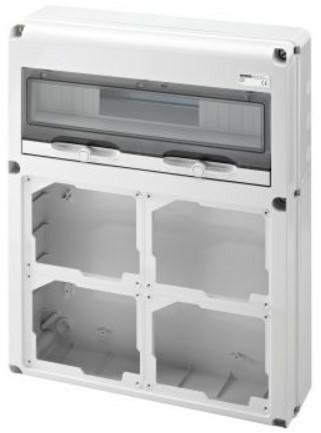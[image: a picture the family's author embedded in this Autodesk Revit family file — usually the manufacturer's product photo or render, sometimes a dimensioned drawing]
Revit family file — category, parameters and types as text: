
# Revit family: Building-IEC309Boards-GEWISS-68QDIN-DISTRIBUTION-BOARD-20MOD_4SOCKET-OUTLETS_IB_ORIZ
name_source: partatom
category: Apparecchi elettrici
units: mm (PartAtom-declared; Revit-internal decimal feet)

## family parameters
Condiviso = No
Host = Superficie
Mantenere orientamento annotazione = Sì
Punto di calcolo locali = Sì
Quota connettore circolare = Usa diametro
Taglio con vuoti quando caricato = No
Tipo di parte = Normale

## types (1)
- GW68014N - Q-DIN 20M 4 FLANGES S.O.BL.HOR.CBF IP65
    Accordance with Standards = EN 60208 - EN 60670-1 - IEC 60670-24
    Catalogue = BUILDING
    Catalogue Range = 68 QDIN
    Colour = Grey RAL 7035
    Descrizione = Q-DIN 20M 4 FLANGES S.O.BL.HOR.CBF IP65
    Dispersible power A (W) = 30
    Dispersible power B (W) = 92
    EAN code = 8011564744837
    Electrocod = 2242
    For socket-outlets = CBF horizontal
    Glow Wire Test = 650°C
    Houseable interloc. socket. = 4 IB Horiz. 16/32A CBF IP44
    Houseable socket = 4 IB Horiz. 16/32A CBF IP44
    IDF = 6844e258-d407-403b-8fb6-669cf0bd49dc
    IDT = 90d6f30b-0b77-4e9c-bb41-47f43079aa94
    IP degree = IP65
    Immagine tipo = GW68014N.jpg
    Installation type = Surface-mounting
    Insulation class = II
    Modello = GW68014N
    No. IB socket-outlets houseable = 4 IB Horiz. 16/32A CBF IP44
    No. of blank lids supplied = 2 IB 16/32A
    No. of modules EN 50022 = 20
    No. of provided blank lids = 2 IB 16/32A
    Operating temperature: = -25 +40 °C
    POMELLO = bianco
    PRESA = rosso
    Produttore = GEWISS S.p.A.
    Prospetto di default = 1219 mm
    SEO = Board
    STRUTTURA = RAL - 7035
    STRUTTURA ALTA = Poche
    Shock resistance = IK08
    Spostamento_S = 1000 mm  [stored 3.28084 ft]
    Technical sheet = https://www.gewiss.com
    Thermo-pressure with ball = 70
    URL = https://www.gewiss.com
    VETRO = Vetro
    Version file RFA = 21.5
    Version type = Empty
    Working temperature = -25 ÷ +40 °C

note: source unit labels omitted for Thermo-pressure with ball — the stored unit's dimension contradicts the parameter name (converter mislabeling)

note: [stored X ft] marks values corroborated as IEEE doubles in the binary element streams (Revit-internal decimal feet)

## geometry (parser evidence)
native form markers: Sweep x3
no freeform markers — native parametric forms only
